# Revit family: result
name_source: partatom
category: Plumbing Fixtures
revit_build: Autodesk Revit 2015 (Build: 20140903_1530(x64)
units: mm (PartAtom-declared; Revit-internal decimal feet)

## types (1)
- Default
    BIMobject category = Toilets
    BIMobject category code = sanitary-toilets
    BIMobject main category = Sanitary
    BIMobject main category code = sanitary
    Brand url = http://www.duravit.com
    Edition number = 1
    GTIN code = https://4053424087931
    Installation instructions = https://pro.duravit.com
    Manufacturer name = DURAVIT
    Product Guid = 54afe3a9-c4d2-4b55-b8aa-f21bf58dff9b
    Product SKU = d-code-wall-hanging-set-453509
    Product data url = https://bimobject.com
    Product family = D-Code
    Product group = toilet kits
    Product name = 453509-D-Code Wall hanging set
    Product url = https://pro.duravit.com
    QR code = http://bimobject.com
    Technical description = https://pro.duravit.com
    Youtube clip = https://pro.duravit.com

## geometry (parser evidence)
native form markers: Sweep x3
no freeform markers — native parametric forms only
